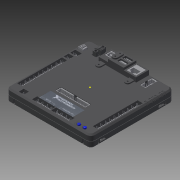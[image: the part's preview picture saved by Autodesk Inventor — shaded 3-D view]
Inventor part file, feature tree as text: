
AUTODESK INVENTOR PART (.ipt)
format: ipt  version: 2018 (Build 220112000, 112)  size: 38,755,840 bytes
history: native  units: in
note: dims shown in document units (in); Inventor stores cm internally (conversion verified against a paired STEP export)
features: imported_body x16, other x3, sketch x2
ambient origin geometry x8: Origin, YZ Plane, XZ Plane, XY Plane, X Axis, Y Axis, Z Axis, Center Point
bodies: Solid1 (feature_tree), Solid2 (feature_tree), Solid3 (feature_tree), Solid4 (feature_tree), Solid5 (feature_tree), Solid6 (feature_tree), Solid7 (feature_tree), Solid8 (feature_tree), Solid9 (feature_tree), Solid10 (feature_tree), Solid11 (feature_tree), Solid12 (feature_tree), Solid13 (feature_tree), Solid14 (feature_tree), Solid15 (feature_tree), Solid16 (feature_tree)
feature tree (21):
  other  "cd_roborio1"
  sketch  "Sketch1"
  other  "Decal2"
  imported_body  "Base1"
  imported_body  "Base2"
  imported_body  "Base3"
  imported_body  "Base4"
  imported_body  "Base5"
  imported_body  "Base6"
  imported_body  "Base7"
  imported_body  "Base8"
  imported_body  "Base9"
  imported_body  "Base10"
  imported_body  "Base11"
  imported_body  "Base12"
  imported_body  "Base13"
  imported_body  "Base14"
  imported_body  "Base15"
  imported_body  "Base16"
  sketch  "Sketch3"
  other  "Image2"
